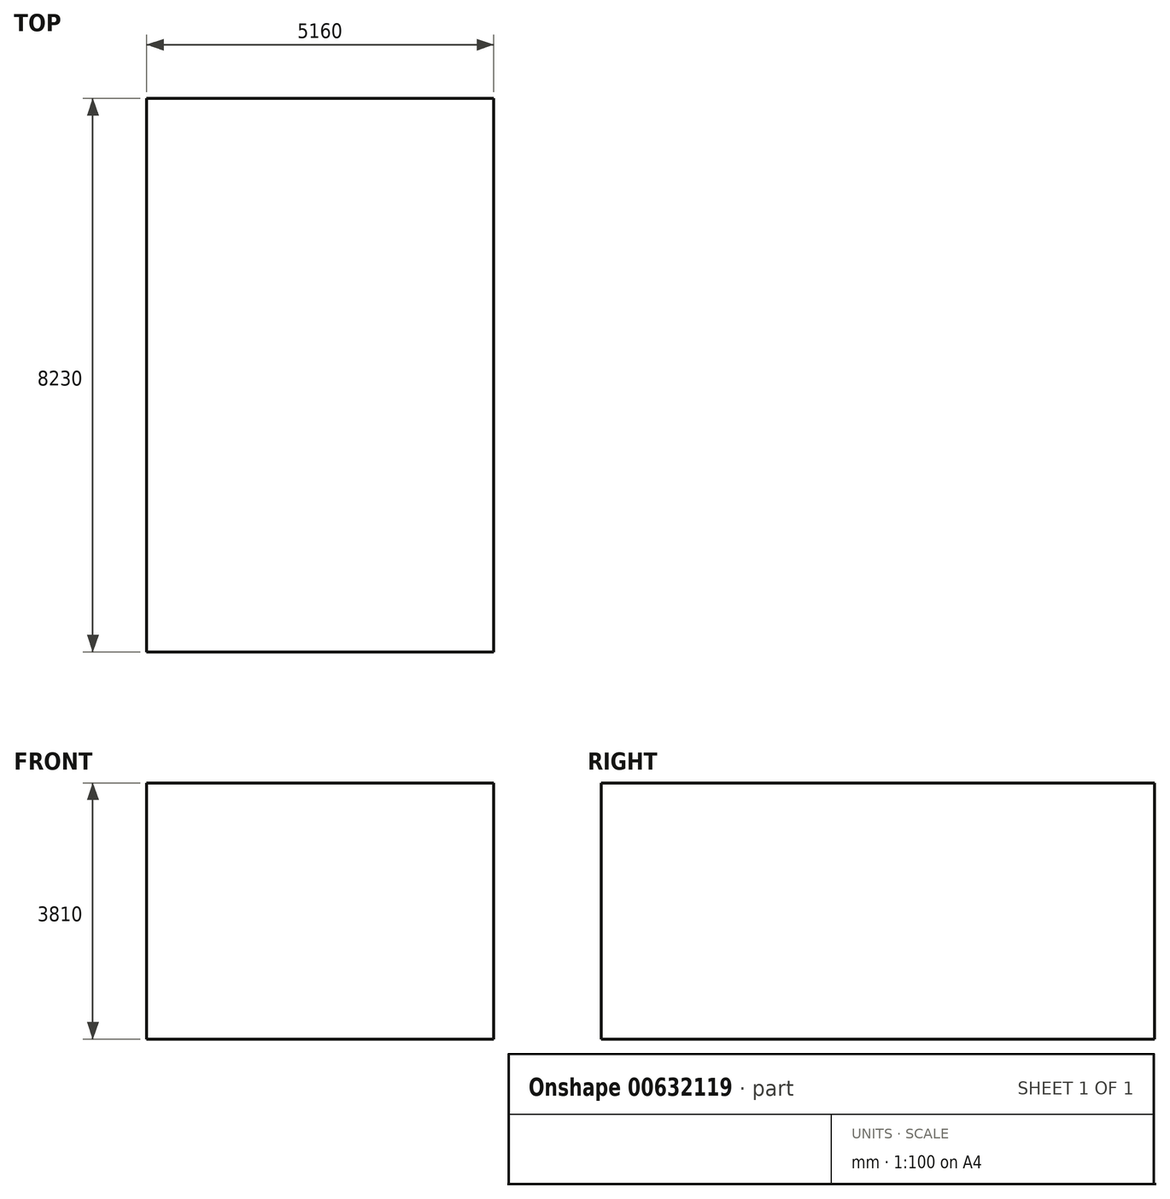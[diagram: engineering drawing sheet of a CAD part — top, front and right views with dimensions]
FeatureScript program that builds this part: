
annotation { "Feature Type Name" : "Feature", "Feature Type Description" : "" }
export const myFeature = defineFeature(function(context is Context, id is Id, definition is map)
    precondition{}
    {
        {
            var Q0;
            Q0=qCreatedBy(makeId("Front.planeOp"),FACE);
            var sketch = newSketch(context, id + "F0", { "sketchPlane" : qUnion([Q0])});
            skLineSegment(sketch, "E0.bottom", {"start": v(0, 0) * mm, "end": v(5160, 0) * mm});
            skLineSegment(sketch, "E0.top", {"start": v(0, 3810) * mm, "end": v(5160, 3810) * mm});
            skLineSegment(sketch, "E0.left", {"start": v(0, 0) * mm, "end": v(0, 3810) * mm});
            skLineSegment(sketch, "E0.right", {"start": v(5160, 0) * mm, "end": v(5160, 3810) * mm});
            skSolve(sketch);
        }
        {
            var Q0;
            Q0 = qSketchRegion(id + "F0", true);
            extrude(context, id + "F1", {"entities" : qUnion([Q0]), "oppositeDirection" : true, "depth" : 8230 * mm, "offsetDistance" : 25.4 * mm});
        }
    });
